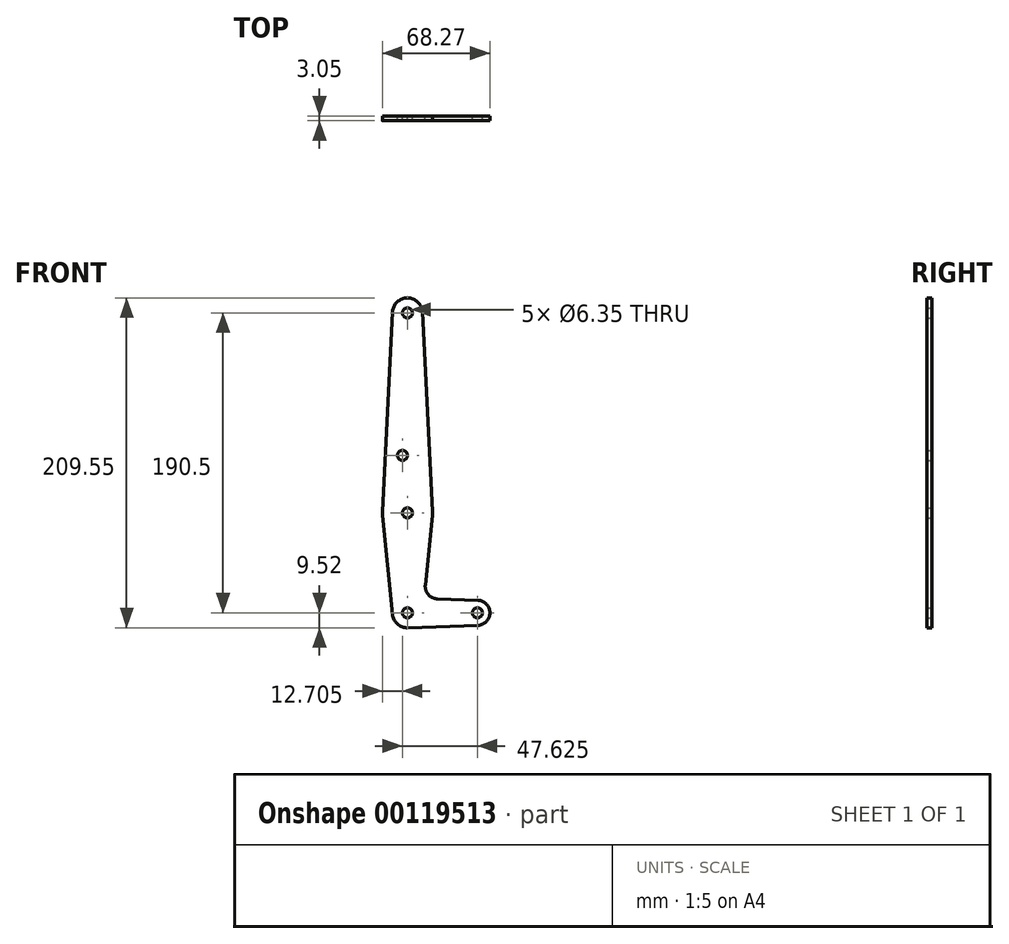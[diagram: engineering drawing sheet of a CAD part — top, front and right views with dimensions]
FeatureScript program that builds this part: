
annotation { "Feature Type Name" : "Feature", "Feature Type Description" : "" }
export const myFeature = defineFeature(function(context is Context, id is Id, definition is map)
    precondition{}
    {
        {
            var Q0;
            Q0=qCreatedBy(makeId("Front.planeOp"),FACE);
            var sketch = newSketch(context, id + "F0", { "sketchPlane" : qUnion([Q0])});
            skCircle(sketch, "E0", {"center": v(0, 0) * mm, "radius": 9.53 * mm});
            skCircle(sketch, "E1", {"center": v(0, 63.5) * mm, "radius": 15.88 * mm});
            skCircle(sketch, "E2", {"center": v(0, 190.5) * mm, "radius": 9.53 * mm});
            skCircle(sketch, "E3", {"center": v(44.45, 0) * mm, "radius": 7.94 * mm});
            skLineSegment(sketch, "E4", {"start": v(0, 0) * mm, "end": v(44.45, 0) * mm, "construction": true});
            skLineSegment(sketch, "E5", {"start": v(0, 190.5) * mm, "end": v(0, 0) * mm, "construction": true});
            skLineSegment(sketch, "E6", {"start": v(-9.51, 190.98) * mm, "end": v(-15.86, 64.3) * mm});
            skLineSegment(sketch, "E7", {"start": v(-15.8, 61.91) * mm, "end": v(-9.48, -0.95) * mm});
            skLineSegment(sketch, "E8", {"start": v(9.51, 190.98) * mm, "end": v(15.86, 64.3) * mm});
            skLineSegment(sketch, "E9", {"start": v(15.8, 61.91) * mm, "end": v(11.34, 17.6) * mm});
            skLineSegment(sketch, "E10", {"start": v(0.34, -9.52) * mm, "end": v(44.73, -7.93) * mm});
            skLineSegment(sketch, "E11", {"start": v(18.97, 8.85) * mm, "end": v(44.73, 7.93) * mm});
            skCircle(sketch, "E12", {"center": v(-3.17, 100.03) * mm, "radius": 3.18 * mm});
            skCircle(sketch, "E13", {"center": v(0, 190.5) * mm, "radius": 3.18 * mm});
            skCircle(sketch, "E14", {"center": v(0, 63.5) * mm, "radius": 3.18 * mm});
            skCircle(sketch, "E15", {"center": v(0, 0) * mm, "radius": 3.18 * mm});
            skCircle(sketch, "E16", {"center": v(44.45, 0) * mm, "radius": 3.18 * mm});
            skArc(sketch, "E17.filletArc", {"start": v(11.34, 17.6) * mm, "mid": v(13.26, 11.57) * mm, "end": v(18.97, 8.85) * mm});
            skSolve(sketch);
        }
        {
            var Q0;
            Q0=makeQuery(id+"F0.imprint","IMPRINT",FACE,{"disambiguationData":[TD([[makeQuery(id+"F0.imprint","IMPRINT",EDGE,{"derivedFrom":sQuery(id+"F0.wireOp",EDGE,"E13")}),-1.0]])]});
            var Q1;
            {var subQ1=sQuery(id+"F0.wireOp",EDGE,"E6");Q1=makeQuery(id+"F0.imprint","IMPRINT",FACE,{"disambiguationData":[TD([[makeQuery(id+"F0.imprint","IMPRINT",EDGE,{"derivedFrom":subQ1}),1.0]])]});}
            var Q2;
            Q2=makeQuery(id+"F0.imprint","IMPRINT",FACE,{"disambiguationData":[TD([[makeQuery(id+"F0.imprint","IMPRINT",EDGE,{"derivedFrom":sQuery(id+"F0.wireOp",EDGE,"E14")}),-1.0]])]});
            var Q3;
            {var subQ0=sQuery(id+"F0.wireOp",EDGE,"E7");Q3=makeQuery(id+"F0.imprint","IMPRINT",FACE,{"disambiguationData":[TD([[makeQuery(id+"F0.imprint","IMPRINT",EDGE,{"derivedFrom":subQ0}),1.0]])]});}
            var Q4;
            Q4=makeQuery(id+"F0.imprint","IMPRINT",FACE,{"disambiguationData":[TD([[makeQuery(id+"F0.imprint","IMPRINT",EDGE,{"derivedFrom":sQuery(id+"F0.wireOp",EDGE,"E15")}),-1.0]])]});
            var Q5;
            Q5=makeQuery(id+"F0.imprint","IMPRINT",FACE,{"disambiguationData":[TD([[makeQuery(id+"F0.imprint","IMPRINT",EDGE,{"derivedFrom":sQuery(id+"F0.wireOp",EDGE,"E16")}),-1.0]])]});
            extrude(context, id + "F1", {"entities" : qUnion([Q0, Q1, Q2, Q3, Q4, Q5]), "depth" : 3.05 * mm});
        }
    });
